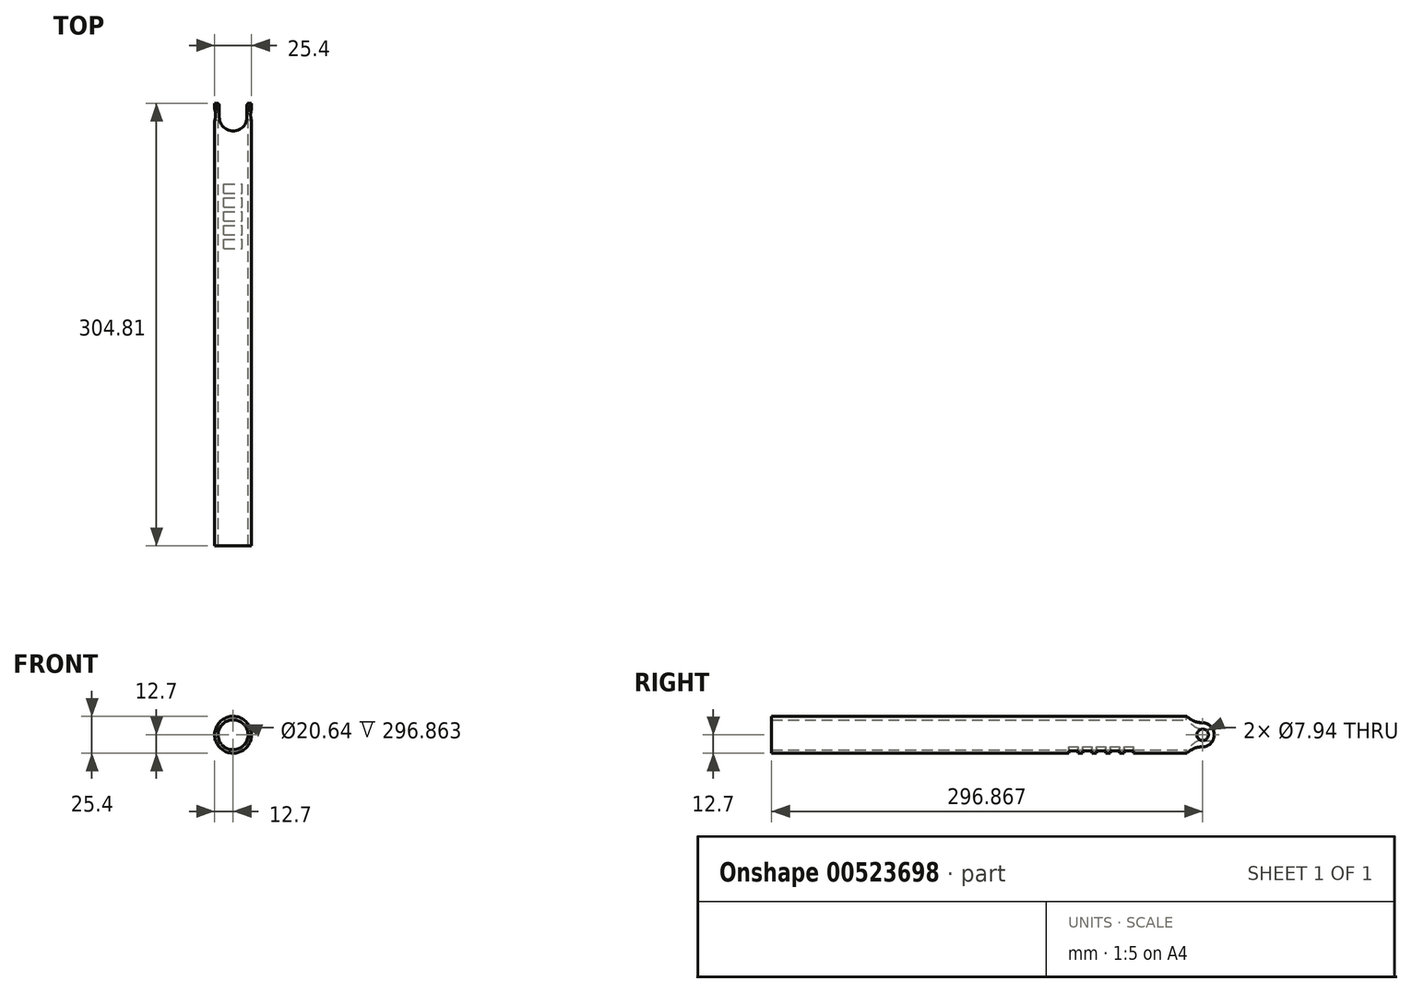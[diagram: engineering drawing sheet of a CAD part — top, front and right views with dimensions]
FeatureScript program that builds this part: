
annotation { "Feature Type Name" : "Feature", "Feature Type Description" : "" }
export const myFeature = defineFeature(function(context is Context, id is Id, definition is map)
    precondition{}
    {
        {
            var Q0;
            Q0=qCreatedBy(makeId("Front.planeOp"),FACE);
            var sketch = newSketch(context, id + "F0", { "sketchPlane" : qUnion([Q0])});
            skCircle(sketch, "E0", {"center": v(0, 0) * mm, "radius": 12.7 * mm});
            skCircle(sketch, "E1", {"center": v(0, 0) * mm, "radius": 10.32 * mm});
            skSolve(sketch);
        }
        {
            var Q0;
            Q0 = qSketchRegion(id + "F0", true);
            extrude(context, id + "F1", {"entities" : qUnion([Q0]), "depth" : 327.02 * mm, "offsetDistance" : 25.4 * mm, "hasSecondDirection" : true, "secondDirectionOppositeDirection" : false, "secondDirectionDepth" : 22.22 * mm});
        }
        {
            var Q0;
            Q0=qCreatedBy(makeId("Top.planeOp"),FACE);
            var sketch = newSketch(context, id + "F2", { "sketchPlane" : qUnion([Q0])});
            skCircle(sketch, "E2", {"center": v(0, -31.75) * mm, "radius": 9.53 * mm});
            skLineSegment(sketch, "E3", {"start": v(-9.53, -31.75) * mm, "end": v(-9.53, -22.23) * mm});
            skLineSegment(sketch, "E4", {"start": v(9.53, -31.75) * mm, "end": v(9.53, -22.23) * mm});
            skLineSegment(sketch, "E5", {"start": v(-9.53, -31.75) * mm, "end": v(9.53, -31.75) * mm, "construction": true});
            skLineSegment(sketch, "E6", {"start": v(-9.53, -22.23) * mm, "end": v(9.53, -22.23) * mm});
            skSolve(sketch);
        }
        {
            var Q0;
            Q0 = qSketchRegion(id + "F2", true);
            extrude(context, id + "F3", {"entities" : qUnion([Q0]), "operationType" : NewBodyOperationType.REMOVE, "endBound" : BoundingType.SYMMETRIC, "oppositeDirection" : true, "depth" : 25.4 * mm, "offsetDistance" : 25.4 * mm});
        }
        {
            var Q0;
            Q0=qCreatedBy(makeId("Right.planeOp"),FACE);
            var sketch = newSketch(context, id + "F4", { "sketchPlane" : qUnion([Q0])});
            skCircle(sketch, "E7", {"center": v(-30.16, 0) * mm, "radius": 3.97 * mm});
            skLineSegment(sketch, "E8", {"start": v(-30.16, 0) * mm, "end": v(-22.23, 0) * mm, "construction": true});
            skSolve(sketch);
        }
        {
            var Q0;
            Q0 = qSketchRegion(id + "F4", true);
            extrude(context, id + "F5", {"entities" : qUnion([Q0]), "operationType" : NewBodyOperationType.REMOVE, "endBound" : BoundingType.SYMMETRIC, "depth" : 25.4 * mm, "offsetDistance" : 25.4 * mm});
        }
        {
            var Q0;
            Q0=qCreatedBy(makeId("Top.planeOp"),FACE);
            var sketch = newSketch(context, id + "F6", { "sketchPlane" : qUnion([Q0])});
            skLineSegment(sketch, "E9", {"start": v(0, 0) * mm, "end": v(0, -96.84) * mm, "construction": true});
            skLineSegment(sketch, "E10.bottom", {"start": v(-6.35, -96.84) * mm, "end": v(6.35, -96.84) * mm});
            skLineSegment(sketch, "E10.top", {"start": v(-6.35, -103.19) * mm, "end": v(6.35, -103.19) * mm});
            skLineSegment(sketch, "E10.left", {"start": v(-6.35, -96.84) * mm, "end": v(-6.35, -103.19) * mm});
            skLineSegment(sketch, "E10.right", {"start": v(6.35, -96.84) * mm, "end": v(6.35, -103.19) * mm});
            skLineSegment(sketch, "E11", {"start": v(0, -96.84) * mm, "end": v(6.35, -96.84) * mm, "construction": true});
            skLineSegment(sketch, "E12", {"start": v(0, -96.84) * mm, "end": v(0, -93.66) * mm, "construction": true});
            skLineSegment(sketch, "E13", {"start": v(0, -103.19) * mm, "end": v(0, -106.36) * mm, "construction": true});
            skLineSegment(sketch, "E14.bottom", {"start": v(-6.35, -106.36) * mm, "end": v(6.35, -106.36) * mm});
            skLineSegment(sketch, "E14.top", {"start": v(-6.35, -112.71) * mm, "end": v(6.35, -112.71) * mm});
            skLineSegment(sketch, "E14.left", {"start": v(-6.35, -106.36) * mm, "end": v(-6.35, -112.71) * mm});
            skLineSegment(sketch, "E14.right", {"start": v(6.35, -106.36) * mm, "end": v(6.35, -112.71) * mm});
            skLineSegment(sketch, "E15.bottom", {"start": v(-6.35, -93.66) * mm, "end": v(6.35, -93.66) * mm});
            skLineSegment(sketch, "E15.top", {"start": v(-6.35, -87.31) * mm, "end": v(6.35, -87.31) * mm});
            skLineSegment(sketch, "E15.left", {"start": v(-6.35, -93.66) * mm, "end": v(-6.35, -87.31) * mm});
            skLineSegment(sketch, "E15.right", {"start": v(6.35, -93.66) * mm, "end": v(6.35, -87.31) * mm});
            skLineSegment(sketch, "E16", {"start": v(0, -112.71) * mm, "end": v(0, -115.89) * mm, "construction": true});
            skLineSegment(sketch, "E17", {"start": v(0, -87.31) * mm, "end": v(0, -84.14) * mm, "construction": true});
            skLineSegment(sketch, "E18.bottom", {"start": v(-6.35, -84.14) * mm, "end": v(6.35, -84.14) * mm});
            skLineSegment(sketch, "E18.top", {"start": v(-6.35, -77.79) * mm, "end": v(6.35, -77.79) * mm});
            skLineSegment(sketch, "E18.left", {"start": v(-6.35, -84.14) * mm, "end": v(-6.35, -77.79) * mm});
            skLineSegment(sketch, "E18.right", {"start": v(6.35, -84.14) * mm, "end": v(6.35, -77.79) * mm});
            skLineSegment(sketch, "E19.bottom", {"start": v(-6.35, -115.89) * mm, "end": v(6.35, -115.89) * mm});
            skLineSegment(sketch, "E19.top", {"start": v(-6.35, -122.24) * mm, "end": v(6.35, -122.24) * mm});
            skLineSegment(sketch, "E19.left", {"start": v(-6.35, -115.89) * mm, "end": v(-6.35, -122.24) * mm});
            skLineSegment(sketch, "E19.right", {"start": v(6.35, -115.89) * mm, "end": v(6.35, -122.24) * mm});
            skSolve(sketch);
        }
        {
            var Q0;
            Q0 = qSketchRegion(id + "F6", true);
            var Q1;
            Q1=sQuery(id+"F6.wireOp",EDGE,"E10.left");
            var Q2;
            Q2=sQuery(id+"F6.wireOp",EDGE,"E10.top");
            var Q3;
            Q3=sQuery(id+"F6.wireOp",EDGE,"E10.right");
            var Q4;
            Q4=sQuery(id+"F6.wireOp",EDGE,"E10.bottom");
            var Q5;
            Q5=makeQuery(id+"F1.opExtrude","SWEPT_FACE",FACE,{"disambiguationData":[OSD([sQuery(id+"F0.wireOp",EDGE,"E0")])]});
            extrude(context, id + "F7", {"entities" : qUnion([Q0]), "operationType" : NewBodyOperationType.REMOVE, "surfaceEntities" : qUnion([Q1, Q2, Q3, Q4]), "endBound" : BoundingType.UP_TO_SURFACE, "oppositeDirection" : true, "depth" : 25.4 * mm, "endBoundEntityFace" : qUnion([Q5]), "offsetDistance" : 25.4 * mm});
        }
        {
            var Q0;
            Q0=qCreatedBy(makeId("Right.planeOp"),FACE);
            var sketch = newSketch(context, id + "F8", { "sketchPlane" : qUnion([Q0])});
            skArc(sketch, "E20", {"start": v(-31.81, -8.4) * mm, "mid": v(-22.24, -0.61) * mm, "end": v(-30.66, 8.4) * mm});
            skLineSegment(sketch, "E21", {"start": v(-30.66, 8.4) * mm, "end": v(-22.23, 8.4) * mm});
            skLineSegment(sketch, "E22", {"start": v(-22.23, -8.4) * mm, "end": v(-31.81, -8.4) * mm});
            skLineSegment(sketch, "E23", {"start": v(-22.23, 0) * mm, "end": v(-30.66, -0.04) * mm, "construction": true});
            skLineSegment(sketch, "E24", {"start": v(-22.23, 8.4) * mm, "end": v(-22.23, -8.4) * mm});
            skSolve(sketch);
        }
        {
            var Q0;
            Q0 = qSketchRegion(id + "F8", true);
            extrude(context, id + "F9", {"entities" : qUnion([Q0]), "operationType" : NewBodyOperationType.REMOVE, "endBound" : BoundingType.SYMMETRIC, "oppositeDirection" : true, "depth" : 38.1 * mm, "offsetDistance" : 25.4 * mm, "hasSecondDirection" : true, "secondDirectionOppositeDirection" : false, "secondDirectionDepth" : 25.4 * mm});
        }
    });
